# Revit family: РВК_Бурт с накидной гайкой
name_source: partatom
category: Соединительные детали трубопроводов
revit_build: Autodesk Revit 2016 (Build: 20150714_1515(x64)
units: mm (PartAtom-declared; Revit-internal decimal feet)

## family parameters
Всегда вертикально = Да
На основе рабочей плоскости = Нет
Общий = Нет
При загрузке вырезать с полостями = Нет
Размер круглого соединителя = Использовать радиус
Тип детали = Соединение

## types (4) — shared parameters
ADSK_Завод-изготовитель = РВК
B-C = 10 мм
Материал стальной части = РВК_Сталь хромированная
Материал фитинга = РВК_Полипропилен PPR

## per-type parameters (varying)
| type | A | B | C | D | DN | E | F | G | H | I | J | L | S | g | r |
| Бурт с накидной гайкой D32-1 1/4'' | 35 мм | 16 мм | 6 мм | 32 мм | 32 мм | 39 мм | 48 мм | 40 мм | 45 мм | 32 мм | 18 мм | 52 мм | 46 мм | 20 мм | 16 мм |
| Бурт с накидной гайкой D25-1'' | 28 мм | 16 мм | 6 мм | 25 мм | 25 мм | 30 мм | 38 мм | 32 мм | 35 мм | 25 мм | 18 мм | 45 мм | 36 мм | 16 мм | 13 мм |
| Бурт с накидной гайкой D20-3/4'' | 28 мм | 15 мм | 5 мм | 20 мм | 20 мм | 24 мм | 31 мм | 25 мм | 28 мм | 20 мм | 17 мм | 45 мм | 30 мм | 13 мм | 10 мм |
| Бурт с накидной гайкой D 16-1/2'' | 23 мм | 14 мм | 4 мм | 16 мм | 16 мм | 19 мм | 26 мм | 20 мм | 24 мм | 16 мм | 16 мм | 39 мм | 24 мм | 10 мм | 8 мм |

note: column(s) folded — value = type name in every type: Type

## geometry (parser evidence)
native form markers: Blend x4
no freeform markers — native parametric forms only
